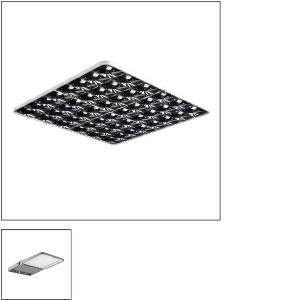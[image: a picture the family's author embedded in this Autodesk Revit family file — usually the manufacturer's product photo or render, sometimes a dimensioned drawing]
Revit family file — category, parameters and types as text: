
# Revit family: siteco_mirrortec_r__indoor___rs05_5nw14091qa_1e52
name_source: partatom
category: Lighting Fixtures
units: mm (PartAtom-declared; Revit-internal decimal feet)

## family parameters
Cut with Voids When Loaded = No
Host = Face
Light Source = No
Part Type = Normal
Room Calculation Point = No
Round Connector Dimension = Use Diameter
Shared = No

## types (1)
- 5XA7682G2H2AC (1 x LED, 34300 lm, 305.7 W, 4000K)
    Apparent Load = 306 VA
    CIE Flux Codes = 47 83 98 49 100
    Color Rendering = 70
    Color Temperature = 4000K
    Default Elevation = 1800 mm
    Description = secondary reflector, for Siteco Mirrortec® Indoor, ball-and-socket joint pendant suspension, housing, square, of aluminium, coated, metallic grey (RAL 9006), fresnel reflector 100, of PMMA, aluminized, highly specular, light point resolution, fresnel structure, length: 600 mm, width: 600 mm

Light Distribution: RS05
    Height = 342 mm
    Lamp = 1 x LED
    Lamp Light Flux = 34300 lm
    Lamp Power = 305.7 W
    Lamp count = 1
    Length = 618 mm
    Luminous efficacy = 112 lm/W
    Manufacturer = Siteco
    ModVariant = No
    Model = 5NW14091QA
    Mounting Place = Ceiling
    Mounting Type = Pendant
    Number of Poles = 1
    OnlyDefault = Yes
    Power Factor = 1
    Product Name = Siteco Mirrortec® Indoor | RS05
    Product group = secondary reflector
    ProductGroupID = 910
    Protection Class = Protection class II
    Protection Degree = IP 66
    RLX_Detail_Level = 1
    RlxData = <blob elided: 104377 chars, md5=54a4bf15>
    Socket = socket
    Standby Power = 0 W
    System Light Flux = 34300 lm
    System Power = 306 W
    Type Comments = Floodlight FL 20 midi, floodlight, primary light control with lens, of plastic, primary optical cover: protective disc, of toughened safety glass, transparent, light distribution: RS05, light emission: direct distribution, primary light characteristic: rotationally symmetric, installation type: surface-mounted, LED High Power LED, rated luminous flux: 38.380 lm, light colour: 740, colour temperature: 4000K, control gear: ECG Plus, control: overheat protection, power reduction, digital communication interface, time-dependent luminous flux control, flexible luminous flux parameterisation, electronic power reduction, with terminal, 10-pole, max. 2.5mm², mains connection: 220..240V, AC, 50/60Hz, rated input power: 306W, LED unit, of diecast aluminium, powder-coated, Siteco® metallic grey (DB 702S), length: 731 mm, width: 450 mm, height: 76mm, housing frame, of diecast aluminium, powder-coated, Siteco® metallic grey (DB 702S), wall fastening, DALIprotection rating (complete): IP66, insulation class (complete): insulation class II (safety insulation), certification: CE, ENEC, VDE, protection symbol: D, permissible ambient temperature for indoor applications: -40..+40°C, permissible ambient temperature for outdoor applications: -40..+50°C, standard: DIN EN 12944, packaging unit: 1 piece

individual setting: distance floodlight mirror = 2,0m / reflector tilt = 5°
    Type Image = l_577132_1005944.jpg
    URL = http://relux.com
    VarID = 5xa7682g2h2ac@adj_128751
    Voltage = 0 V
    Weight = 0.00 kg
    Width = 618 mm

## geometry (parser evidence)
native form markers: Blend x4, Sweep x9
no freeform markers — native parametric forms only
